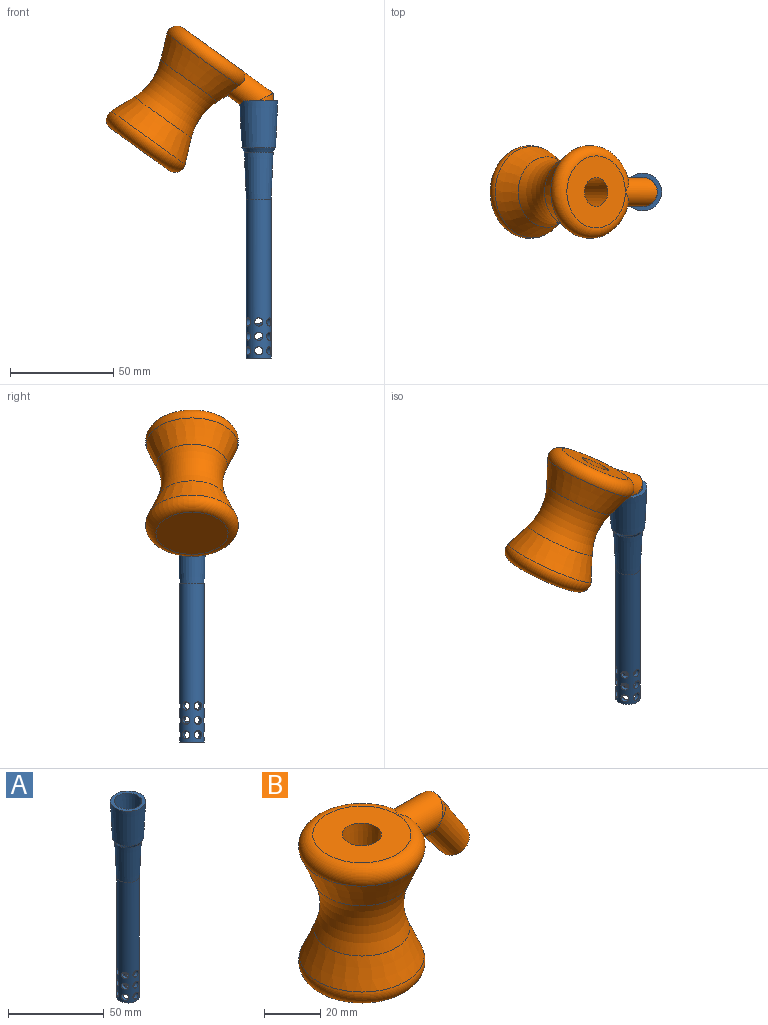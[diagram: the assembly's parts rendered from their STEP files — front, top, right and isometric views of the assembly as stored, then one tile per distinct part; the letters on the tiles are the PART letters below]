
ASSEMBLY  parts=2 mates=1
PART A: 34 faces, bbox 18.4x18.4x125 mm
  f0: cylinder r=4mm len=8mm, axis (0,0,1), area 37mm2, adj f1,f2,f3,f4,f5,f6
  f1: cylinder r=2mm len=4.73mm, axis (0.87,0.5,0), area 26.3mm2, adj f0,f2,f6,f7,f8
  f2: cylinder r=2mm len=4.73mm, axis (-0.87,0.5,0), area 26.3mm2, adj f0,f1,f3,f7,f8
  f3: cylinder r=2mm len=4mm, axis (0,-1,0), area 26.3mm2, adj f0,f2,f4,f7,f8
  f4: cylinder r=2mm len=4.73mm, axis (0.87,0.5,0), area 26.3mm2, adj f0,f3,f5,f7,f8
  f5: cylinder r=2mm len=4.73mm, axis (-0.87,0.5,0), area 26.3mm2, adj f0,f4,f6,f7,f8
  f6: cylinder r=2mm len=4mm, axis (0,-1,0), area 26.3mm2, adj f0,f1,f5,f7,f8
  f7: cylinder r=6mm len=77mm, axis (0,0,1), area 2673.6mm2, adj f1,f2,f3,f4,f5,f6,f9,f10
  f8: cylinder r=4mm len=8mm, axis (0,0,1), area 37mm2, adj f1,f2,f3,f4,f5,f6
  f9: plane 12x12mm, normal (0,0,-1), area 62.9mm2, adj f7,f23
  f10: cone r=6mm half-angle=2.5deg, axis (0,0,1), area 939.3mm2, adj f7,f24
  f11: cylinder r=2mm len=4mm, axis (0,-1,0), area 26.3mm2, adj f7,f12,f13,f25,f26
  f12: cylinder r=2mm len=4.73mm, axis (-0.87,0.5,0), area 26.3mm2, adj f7,f11,f16,f25,f26
  f13: cylinder r=2mm len=4.73mm, axis (0.87,0.5,0), area 26.3mm2, adj f7,f11,f14,f25,f26
  f14: cylinder r=2mm len=4.73mm, axis (-0.87,0.5,0), area 26.3mm2, adj f7,f13,f15,f25,f26
  f15: cylinder r=2mm len=4mm, axis (0,-1,0), area 26.3mm2, adj f7,f14,f16,f25,f26
  f16: cylinder r=2mm len=4.73mm, axis (0.87,0.5,0), area 26.3mm2, adj f7,f12,f15,f25,f26
  f17: cylinder r=2mm len=4mm, axis (0,-1,0), area 26.3mm2, adj f7,f19,f22,f23,f27
  f18: cylinder r=2mm len=4.73mm, axis (0.87,0.5,0), area 26.3mm2, adj f7,f19,f20,f23,f27
  f19: cylinder r=2mm len=4.73mm, axis (-0.87,0.5,0), area 26.3mm2, adj f7,f17,f18,f23,f27
  f20: cylinder r=2mm len=4mm, axis (0,-1,0), area 26.3mm2, adj f7,f18,f21,f23,f27
  f21: cylinder r=2mm len=4.73mm, axis (-0.87,0.5,0), area 26.3mm2, adj f7,f20,f22,f23,f27
  f22: cylinder r=2mm len=4.73mm, axis (0.87,0.5,0), area 26.3mm2, adj f7,f17,f21,f23,f27
  f23: cylinder r=4mm len=8mm, axis (0,0,1), area 48.9mm2, adj f9,f17,f18,f19,f20,f21,f22
  f24: cone r=8.2mm half-angle=30.7deg, axis (0,0,1), area 112.3mm2, adj f10,f28
  f25: cylinder r=4mm len=8mm, axis (0,0,1), area 37mm2, adj f11,f12,f13,f14,f15,f16
  f26: cylinder r=4mm len=8mm, axis (0,0,1), area 37mm2, adj f11,f12,f13,f14,f15,f16
  f27: cylinder r=4mm len=8mm, axis (0,0,1), area 37mm2, adj f17,f18,f19,f20,f21,f22
  f28: cone r=9.2mm half-angle=2.5deg, axis (0,0,1), area 1257.5mm2, adj f24,f29
  f29: plane 18.4x18.4mm, normal (0,0,1), area 103.2mm2, adj f28,f30
  f30: cone r=7.2mm half-angle=2.5deg, axis (0,0,1), area 968.2mm2, adj f29,f31
  f31: cone r=6.2mm half-angle=30.7deg, axis (0,0,1), area 82.7mm2, adj f30,f32
  f32: cone r=5mm half-angle=2.5deg, axis (0,0,1), area 650mm2, adj f31,f33
  f33: cylinder r=4mm len=8mm, axis (0,0,1), area 0mm2, adj f32
PART B: 28 faces, bbox 76.3x50.1x60 mm
  f0: cylinder r=5mm len=21mm, axis (-1,0,0), area 478mm2, adj f3,f5,f6,f8,f10,f24,f26,f27
  f1: cylinder r=7mm len=19.02mm, axis (-1,0,0), area 568.8mm2, adj f4,f5,f15,f23
  f2: plane 12x9.73mm, normal (0.59,0,-0.81), area 62.9mm2, adj f6,f24
  f3: cylinder r=5mm len=10mm, axis (-0.59,0,0.81), area 25.6mm2, adj f0,f25
  f4: cylinder r=7mm len=14mm, axis (-0.59,0,0.81), area 50.1mm2, adj f1,f6
  f5: cylinder r=7mm len=14mm, axis (0.59,0,-0.81), area 44.5mm2, adj f0,f1,f6
  f6: cone r=6mm half-angle=2.5deg, axis (-0.59,0,0.81), area 934.4mm2, adj f0,f2,f4,f5
  f7: cone r=8.91mm half-angle=2.5deg, axis (0,0,1), area 1116mm2, adj f9,f18
  f8: torus R=14.5mm, axis (0,0,-1), area 1043mm2, adj f0,f9,f10
  f9: plane 29x29mm, normal (0,0,-1), area 410.8mm2, adj f7,f8
  f10: cone r=10.33mm half-angle=22.6deg, axis (0,0,1), area 1149.3mm2, adj f0,f8,f20
  f11: cone r=22mm half-angle=22.6deg, axis (0,0,-1), area 1171.7mm2, adj f20,f21
  f12: plane 29x29mm, normal (0,0,1), area 660.5mm2, adj f21
  f13: plane 35x35mm, normal (0,0,-1), area 962.1mm2, adj f22
  f14: cone r=25mm half-angle=22.6deg, axis (0,0,-1), area 1616.4mm2, adj f19,f22
  f15: cone r=25mm half-angle=22.6deg, axis (0,0,1), area 1530.6mm2, adj f1,f19,f23
  f16: plane 35x35mm, normal (0,0,1), area 808.2mm2, adj f17,f23
  f17: cone r=7mm half-angle=2.5deg, axis (0,0,1), area 939.3mm2, adj f16,f18
  f18: plane 16x16mm, normal (0,0,-1), area 88.1mm2, adj f7,f17
  f19: torus R=43.36mm, axis (0,0,1), area 2205.5mm2, adj f14,f15
  f20: torus R=41.19mm, axis (0,0,-1), area 1899.3mm2, adj f10,f11
  f21: torus R=14.5mm, axis (0,0,1), area 1112.9mm2, adj f11,f12
  f22: torus R=17.5mm, axis (0,0,1), area 1298.1mm2, adj f13,f14
  f23: torus R=17.5mm, axis (0,0,1), area 1207.6mm2, adj f1,f15,f16
  f24: cone r=5mm half-angle=2.5deg, axis (-0.59,0,0.81), area 623.3mm2, adj f0,f2,f25,f26,f27
  f25: plane 10x4.05mm, normal (-0.59,0,0.81), area 0mm2, adj f3,f24,f26,f27
  f26: plane 0.58x0.04mm, normal (-1,0,0), area 0mm2, adj f0,f24,f25
  f27: plane 0.58x0.04mm, normal (-1,0,0), area 0mm2, adj f0,f24,f25
PLACE A t=(-30.24,-27.06,-16.95)mm
PLACE B rot(axis=(0,1,0),35.8deg) t=(-87.97,-27.06,36.97)mm
MATE revolute B.f24 <-> A.f0  axis (0,0,1) through (-30.24,-27.06,37.67)mm
